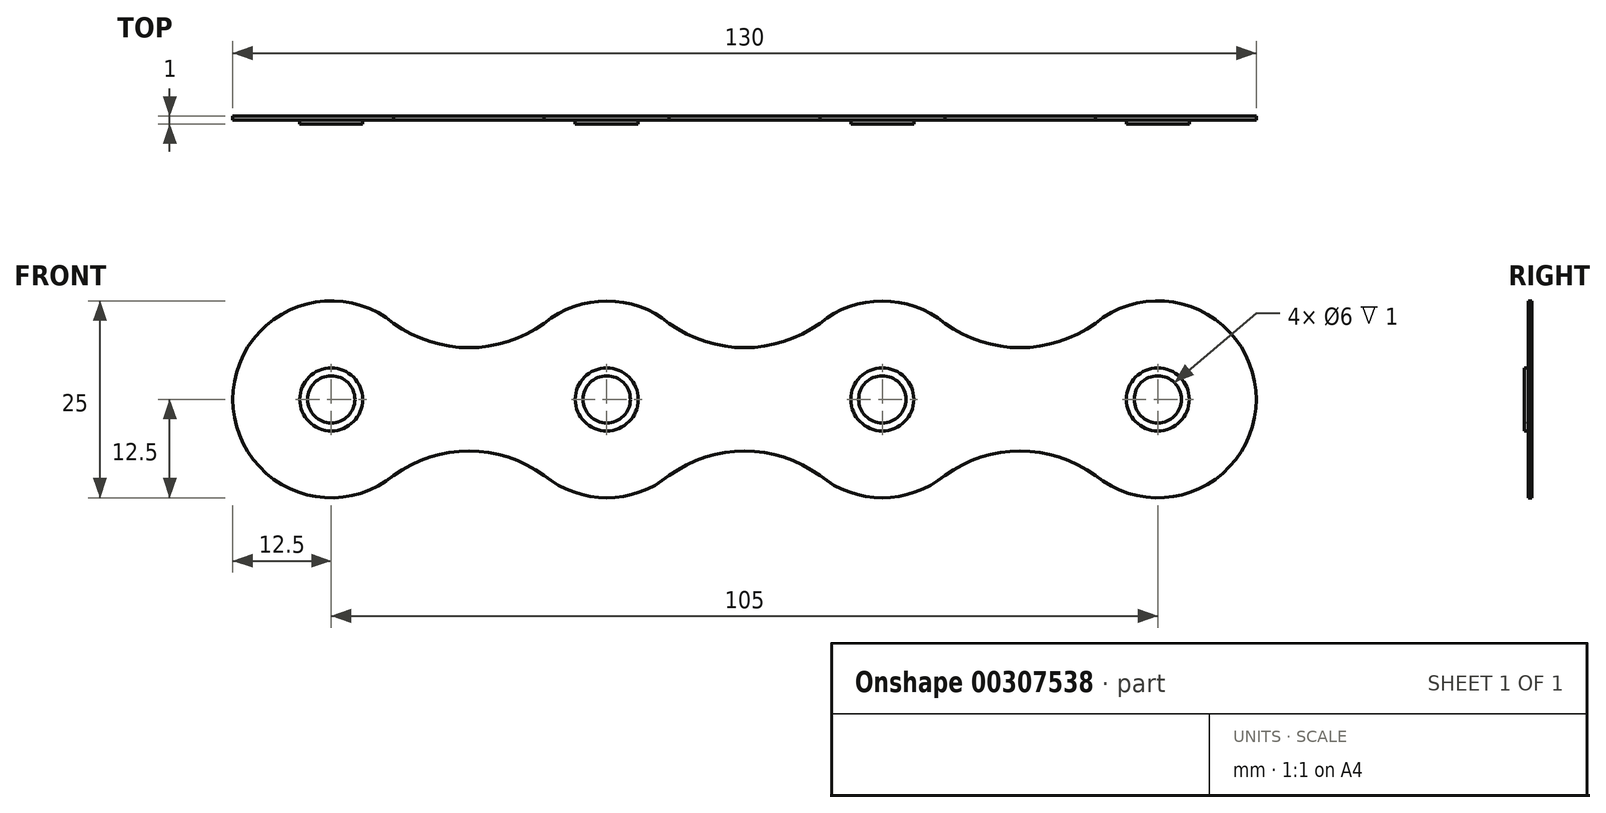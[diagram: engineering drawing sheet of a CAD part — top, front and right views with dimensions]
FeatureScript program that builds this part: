
annotation { "Feature Type Name" : "Feature", "Feature Type Description" : "" }
export const myFeature = defineFeature(function(context is Context, id is Id, definition is map)
    precondition{}
    {
        {
            var Q0;
            Q0=qCreatedBy(makeId("Front.planeOp"),FACE);
            cPlane(context, id + "F0", {"entities" : qUnion([Q0]), "cplaneType" : CPlaneType.OFFSET, "offset" : 1.5 * mm, "width" : 150 * mm, "height" : 150 * mm});
        }
        {
            var Q0;
            Q0=qCreatedBy(makeId("Front.planeOp"),FACE);
            var sketch = newSketch(context, id + "F1", { "sketchPlane" : qUnion([Q0])});
            skCircle(sketch, "E0", {"center": v(0, 0) * mm, "radius": 12.5 * mm});
            skSolve(sketch);
        }
        {
            var Q0;
            Q0=qCreatedBy(id+"F0.planeOp",FACE);
            var sketch = newSketch(context, id + "F2", { "sketchPlane" : qUnion([Q0])});
            skCircle(sketch, "E1", {"center": v(0, 0) * mm, "radius": 2.7 * mm});
            skSolve(sketch);
        }
        {
            var Q0;
            Q0=qCreatedBy(makeId("Front.planeOp"),FACE);
            var sketch = newSketch(context, id + "F3", { "sketchPlane" : qUnion([Q0])});
            skCircle(sketch, "E2", {"center": v(0, 0) * mm, "radius": 3 * mm});
            skSolve(sketch);
        }
        {
            var Q0;
            Q0 = qSketchRegion(id + "F1", true);
            extrude(context, id + "F4", {"entities" : qUnion([Q0]), "depth" : 0.5 * mm, "offsetDistance" : 25 * mm});
        }
        {
            var Q0;
            Q0=makeQuery(id+"F4.opExtrude","CAP_FACE",FACE,{"disambiguationData":[OSD([sQuery(id+"F1.wireOp",EDGE,"E0")])],"isStart":false});
            var sketch = newSketch(context, id + "F5", { "sketchPlane" : qUnion([Q0])});
            skCircle(sketch, "E3", {"center": v(0, 0) * mm, "radius": 4 * mm});
            skSolve(sketch);
        }
        {
            var Q0;
            Q0 = qSketchRegion(id + "F5", true);
            extrude(context, id + "F6", {"entities" : qUnion([Q0]), "operationType" : NewBodyOperationType.ADD, "depth" : 0.5 * mm, "offsetDistance" : 25 * mm});
        }
        {
            var Q0;
            Q0=makeQuery(id+"F6.opExtrude","CAP_FACE",FACE,{"disambiguationData":[OSD([sQuery(id+"F5.wireOp",EDGE,"E3")])],"isStart":false});
            var sketch = newSketch(context, id + "F7", { "sketchPlane" : qUnion([Q0])});
            skCircle(sketch, "E4", {"center": v(0, 0) * mm, "radius": 3 * mm});
            skSolve(sketch);
        }
        {
            var Q1;
            Q1=makeQuery(id+"F3.imprint","IMPRINT",FACE,{"disambiguationData":[TD([[makeQuery(id+"F3.imprint","IMPRINT",EDGE,{"derivedFrom":sQuery(id+"F3.wireOp",EDGE,"E2")}),1.0]])]});
            var Q2;
            Q2=makeQuery(id+"F2.imprint","IMPRINT",FACE,{"disambiguationData":[TD([[makeQuery(id+"F2.imprint","IMPRINT",EDGE,{"derivedFrom":sQuery(id+"F2.wireOp",EDGE,"E1")}),1.0]])]});
            loft(context, id + "F8", {"operationType" : NewBodyOperationType.REMOVE, "sheetProfilesArray" : [{ "sheetProfileEntities" : qUnion([Q1]) }, { "sheetProfileEntities" : qUnion([Q2]) }]});
        }
        {
            var Q0;
            Q0=makeQuery(id+"F7.imprint","IMPRINT",FACE,{"disambiguationData":[TD([[makeQuery(id+"F7.imprint","IMPRINT",EDGE,{"derivedFrom":sQuery(id+"F7.wireOp",EDGE,"E4")}),1.0]])]});
            var Q1;
            Q1=sQuery(id+"F7.wireOp",EDGE,"E4");
            extrude(context, id + "F9", {"entities" : qUnion([Q0]), "operationType" : NewBodyOperationType.REMOVE, "surfaceEntities" : qUnion([Q1]), "oppositeDirection" : true, "depth" : 25 * mm, "offsetDistance" : 25 * mm});
        }
        {
            var Q0;
            Q0=makeQuery(id+"F4.opExtrude","SWEPT_BODY",BODY,{"disambiguationData":[OSD([sQuery(id+"F1.wireOp",EDGE,"E0")])]});
            transform(context, id + "F10", {"entities" : qUnion([Q0]), "transformType" : TransformType.TRANSLATION_3D, "dx" : 35 * mm, "dy" : 0 * mm, "dz" : 0 * mm, "makeCopy" : true});
        }
        {
            var Q0;
            Q0=makeQuery(id+"F4.opExtrude","SWEPT_BODY",BODY,{"disambiguationData":[OSD([sQuery(id+"F1.wireOp",EDGE,"E0")])]});
            transform(context, id + "F11", {"entities" : qUnion([Q0]), "transformType" : TransformType.TRANSLATION_3D, "dx" : 105 * mm, "dy" : 0 * mm, "dz" : 0 * mm, "makeCopy" : true});
        }
        {
            var Q0;
            Q0=makeQuery(id+"F4.opExtrude","SWEPT_BODY",BODY,{"disambiguationData":[OSD([sQuery(id+"F1.wireOp",EDGE,"E0")])]});
            transform(context, id + "F12", {"entities" : qUnion([Q0]), "transformType" : TransformType.TRANSLATION_3D, "dx" : 70 * mm, "dy" : 0 * mm, "dz" : 0 * mm, "makeCopy" : true});
        }
        {
            var Q0;
            Q0=qCreatedBy(makeId("Front.planeOp"),FACE);
            var sketch = newSketch(context, id + "F13", { "sketchPlane" : qUnion([Q0])});
            skArc(sketch, "E5", {"start": v(7.93, 9.66) * mm, "mid": v(17.5, 6.57) * mm, "end": v(27.07, 9.66) * mm});
            skArc(sketch, "E6.1.0.0", {"start": v(42.93, 9.66) * mm, "mid": v(52.5, 6.57) * mm, "end": v(62.07, 9.66) * mm});
            skArc(sketch, "E6.2.0.0", {"start": v(77.93, 9.66) * mm, "mid": v(87.5, 6.57) * mm, "end": v(97.07, 9.66) * mm});
            skLineSegment(sketch, "E6.direction1", {"start": v(7.93, 9.66) * mm, "end": v(42.93, 9.66) * mm, "construction": true});
            skArc(sketch, "E7.MirrorCS", {"start": v(77.93, -9.66) * mm, "mid": v(87.5, -6.57) * mm, "end": v(97.07, -9.66) * mm});
            skArc(sketch, "E8.MirrorCS", {"start": v(7.93, -9.66) * mm, "mid": v(17.5, -6.57) * mm, "end": v(27.07, -9.66) * mm});
            skArc(sketch, "E9.MirrorCS", {"start": v(42.93, -9.66) * mm, "mid": v(52.5, -6.57) * mm, "end": v(62.07, -9.66) * mm});
            skLineSegment(sketch, "E10", {"start": v(7.93, 9.66) * mm, "end": v(7.93, -9.66) * mm});
            skLineSegment(sketch, "E11", {"start": v(27.07, 9.66) * mm, "end": v(27.07, -9.66) * mm});
            skLineSegment(sketch, "E12", {"start": v(42.93, 9.66) * mm, "end": v(42.93, -9.66) * mm});
            skLineSegment(sketch, "E13", {"start": v(62.07, 9.66) * mm, "end": v(62.07, -9.66) * mm});
            skLineSegment(sketch, "E14", {"start": v(77.93, 9.66) * mm, "end": v(77.93, -9.66) * mm});
            skLineSegment(sketch, "E15", {"start": v(97.07, 9.66) * mm, "end": v(97.07, -9.66) * mm});
            skSolve(sketch);
        }
        {
            var Q0;
            Q0=makeQuery(id+"F13.imprint","IMPRINT",FACE,{"disambiguationData":[TD([[makeQuery(id+"F13.imprint","IMPRINT",EDGE,{"derivedFrom":sQuery(id+"F13.wireOp",EDGE,"E5")}),-1.0]])]});
            var Q1;
            Q1=makeQuery(id+"F13.imprint","IMPRINT",FACE,{"disambiguationData":[TD([[makeQuery(id+"F13.imprint","IMPRINT",EDGE,{"derivedFrom":sQuery(id+"F13.wireOp",EDGE,"E6.1.0.0")}),-1.0]])]});
            var Q2;
            Q2=makeQuery(id+"F13.imprint","IMPRINT",FACE,{"disambiguationData":[TD([[makeQuery(id+"F13.imprint","IMPRINT",EDGE,{"derivedFrom":sQuery(id+"F13.wireOp",EDGE,"E6.2.0.0")}),-1.0]])]});
            var Q3;
            Q3=sQuery(id+"F13.wireOp",EDGE,"E5");
            var Q4;
            Q4=sQuery(id+"F13.wireOp",EDGE,"E9.MirrorCS");
            var Q5;
            Q5=sQuery(id+"F13.wireOp",EDGE,"E8.MirrorCS");
            var Q6;
            Q6=sQuery(id+"F13.wireOp",EDGE,"E10");
            var Q7;
            Q7=sQuery(id+"F13.wireOp",EDGE,"E7.MirrorCS");
            var Q8;
            Q8=sQuery(id+"F13.wireOp",EDGE,"E6.1.0.0");
            var Q9;
            Q9=sQuery(id+"F13.wireOp",EDGE,"E11");
            var Q10;
            Q10=sQuery(id+"F13.wireOp",EDGE,"E6.2.0.0");
            var Q11;
            Q11=sQuery(id+"F13.wireOp",EDGE,"E12");
            var Q12;
            Q12=sQuery(id+"F13.wireOp",EDGE,"E13");
            var Q13;
            Q13=sQuery(id+"F13.wireOp",EDGE,"E14");
            var Q14;
            Q14=sQuery(id+"F13.wireOp",EDGE,"E15");
            extrude(context, id + "F14", {"entities" : qUnion([Q0, Q1, Q2]), "operationType" : NewBodyOperationType.ADD, "surfaceEntities" : qUnion([Q3, Q4, Q5, Q6, Q7, Q8, Q9, Q10, Q11, Q12, Q13, Q14]), "depth" : 0.5 * mm, "offsetDistance" : 25 * mm});
        }
    });
